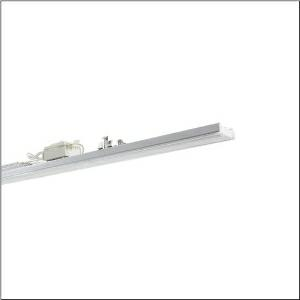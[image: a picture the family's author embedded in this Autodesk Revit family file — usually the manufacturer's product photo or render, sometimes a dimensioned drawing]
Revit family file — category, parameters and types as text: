
# Revit family: licross_11_recessed_ho_51tl11mv4hxs
name_source: partatom
category: Lighting Fixtures
units: mm (PartAtom-declared; Revit-internal decimal feet)

## family parameters
Cut with Voids When Loaded = No
Host = Face
Light Source = No
Part Type = Normal
Room Calculation Point = No
Round Connector Dimension = Use Diameter
Shared = No

## types (1)
- --- (1 x LED, 17230 lm, 89.2 W, 4000K)
    Apparent Load = 89 VA
    CIE Flux Codes = 87 95 99 100 100
    Color Rendering = 80
    Color Temperature = 4000K
    Default Elevation = 1800 mm
    Description = Licross 11 Recessed HO, luminaire insert, of sheet steel, coil coated, white, length: 2.250mm, width: 66mm, height: 67mm, LED rated luminous flux: 17.230lm, light colour: 840, SDCM (Standard Deviation of Colour Matching)MacAdam ≤ 2 SDCM (initial), control gear: ON/OFF Multilumen, with plug, 3-pole, with phase selection, mains connection: 220..240V, AC, 50/60Hz, rated input power: 89W, internal wiring halogen-free, primary light control with lens, of plastic, primary optical cover: cover, of PMMA, light emission: direct distribution, primary light characteristic: symmetric, protection rating (complete): IP40, insulation class (complete): insulation class I (protective earthing), certification: CE, ENEC, VDE, UKCA, protection symbol: D if used in an environment without relevant dust loads with corresponding accessories, impact resistance: IK06, permissible ambient temperature for indoor applications: -35..+35°C, corresponds to IFS (International Featured Standards) requirements for safety and quality in the food industry, reducing of maximum allowable ambient temperature of 5°C with ceiling mounting, The light source and the operating device comply with the requirements of the Ecodesign Regulation (EU) 2019/2020 and are replaceable in accordance with this regulation, packaging unit: 1 piece
    Height = 58 mm
    Lamp = 1 x LED
    Lamp Light Flux = 17230 lm
    Lamp Power = 89.2 W
    Lamp count = 1
    Length = 2250 mm
    Luminous efficacy = 193 lm/W
    Manufacturer = Siteco
    ModVariant = No
    Model = 51TL11MV4HXS
    Mounting Place = Ceiling
    Mounting Type = Pendant
    Number of Poles = 1
    OnlyDefault = Yes
    Power Factor = 1
    Product Name = Licross 11 Recessed HO
    Product group = luminaire insert | ceiling pendant
    ProductGroupID = 901
    Protection Class = Protection class I
    Protection Degree = IP 40
    RLX_Detail_Level = 1
    RLX_Emergency_Light_Flux = 0 lm
    RLX_Emergency_Type = 0
    RLX_Emergency_Type_DB = No
    RlxData = <blob elided: 27189 chars, md5=b826c2e8>
    Socket = socket
    Standby Power = 0 W
    System Light Flux = 17230 lm
    System Power = 89 W
    Type Comments = factory setting: luminous flux: 100 % | (A | C | E) | 210 mA
    Type Image = l_1296930.jpg
    URL = http://relux.com
    VarID = @adj_089467
    Voltage = 0 V
    Weight = 0.00 kg
    Width = 66 mm

## geometry (parser evidence)
native form markers: Blend x4, Sweep x10
no freeform markers — native parametric forms only
